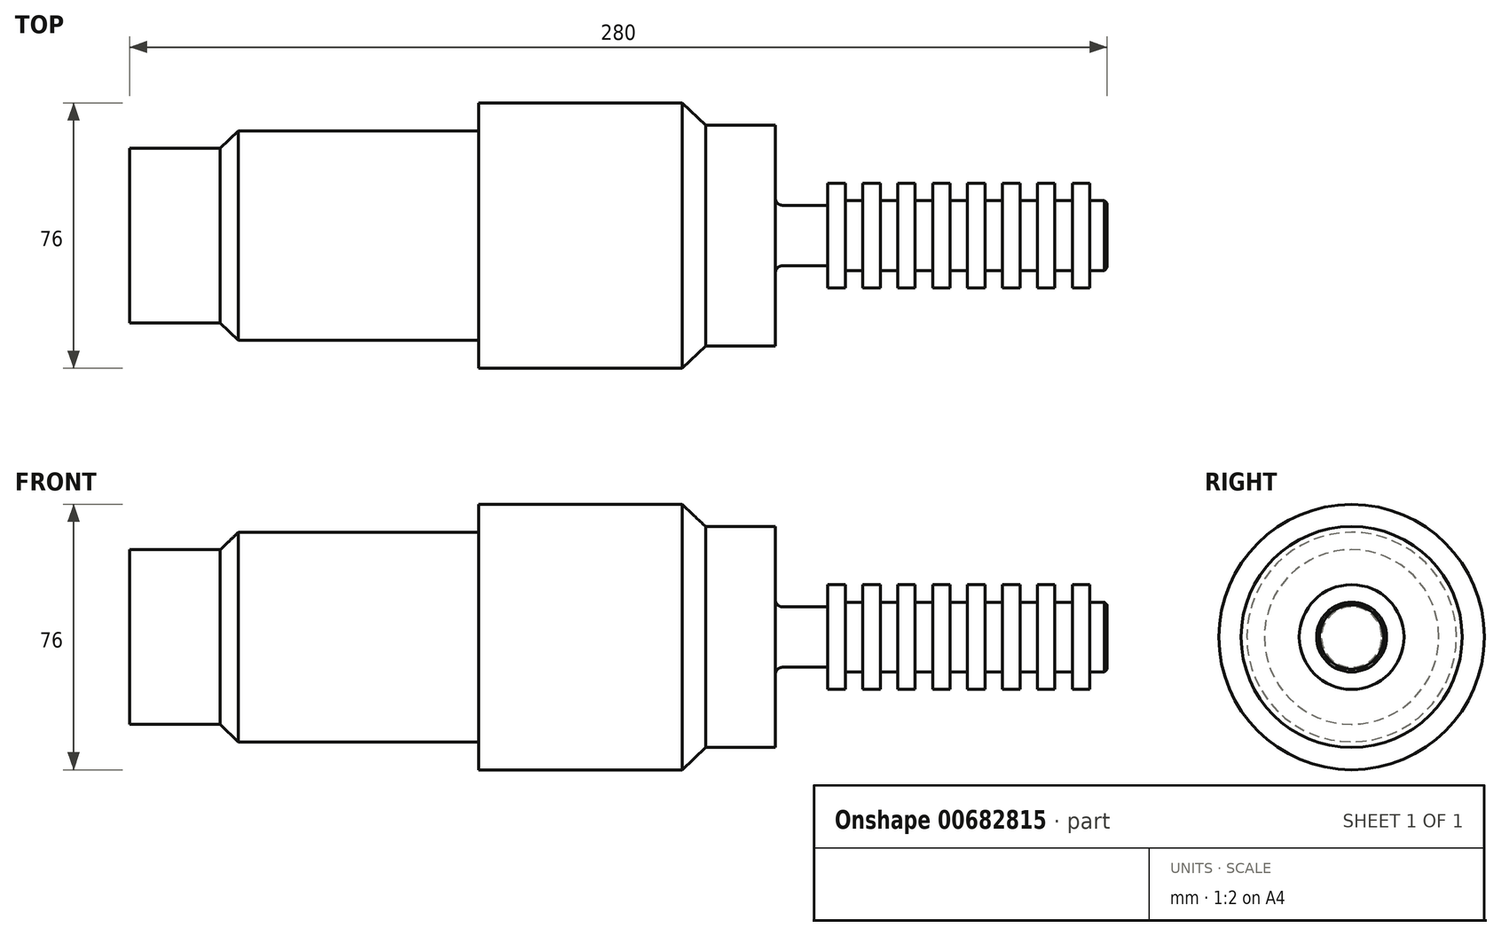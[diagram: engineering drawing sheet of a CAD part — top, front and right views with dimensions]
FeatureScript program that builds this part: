
annotation { "Feature Type Name" : "Feature", "Feature Type Description" : "" }
export const myFeature = defineFeature(function(context is Context, id is Id, definition is map)
    precondition{}
    {
        {
            var Q0;
            Q0=qCreatedBy(makeId("Front.planeOp"),FACE);
            var sketch = newSketch(context, id + "F0", { "sketchPlane" : qUnion([Q0])});
            skLineSegment(sketch, "E0", {"start": v(-57.6, 0) * mm, "end": v(222.4, 0) * mm});
            skLineSegment(sketch, "E1", {"start": v(-57.6, 0) * mm, "end": v(-57.6, 25) * mm});
            skLineSegment(sketch, "E2", {"start": v(-57.6, 25) * mm, "end": v(-31.6, 25) * mm});
            skLineSegment(sketch, "E3", {"start": v(-26.44, 30) * mm, "end": v(42.4, 30) * mm});
            skLineSegment(sketch, "E4", {"start": v(42.4, 30) * mm, "end": v(42.4, 38) * mm});
            skLineSegment(sketch, "E5", {"start": v(42.4, 38) * mm, "end": v(100.66, 38) * mm});
            skLineSegment(sketch, "E6", {"start": v(107.4, 31.64) * mm, "end": v(127.4, 31.64) * mm});
            skLineSegment(sketch, "E7", {"start": v(127.4, 31.64) * mm, "end": v(127.4, 15) * mm});
            skLineSegment(sketch, "E8", {"start": v(222.4, 9.2) * mm, "end": v(222.4, 0) * mm});
            skLineSegment(sketch, "E9", {"start": v(107.4, 31.64) * mm, "end": v(100.66, 38) * mm});
            skLineSegment(sketch, "E10", {"start": v(-31.6, 25) * mm, "end": v(-26.44, 30) * mm});
            skLineSegment(sketch, "E11", {"start": v(217.4, 15) * mm, "end": v(217.4, 10) * mm});
            skLineSegment(sketch, "E12", {"start": v(217.4, 10) * mm, "end": v(221.6, 10) * mm});
            skLineSegment(sketch, "E13", {"start": v(212.4, 15) * mm, "end": v(212.4, 10) * mm});
            skLineSegment(sketch, "E14", {"start": v(212.4, 10) * mm, "end": v(207.4, 10) * mm});
            skLineSegment(sketch, "E15", {"start": v(207.4, 10) * mm, "end": v(207.4, 15) * mm});
            skPoint(sketch, "E16.orphan", {"position": v(222.4, 15) * mm});
            skLineSegment(sketch, "E17.trimOffspring", {"start": v(212.4, 15) * mm, "end": v(217.4, 15) * mm});
            skLineSegment(sketch, "E18", {"start": v(202.4, 15) * mm, "end": v(202.4, 10) * mm});
            skLineSegment(sketch, "E19", {"start": v(202.4, 10) * mm, "end": v(197.4, 10) * mm});
            skLineSegment(sketch, "E20", {"start": v(197.4, 10) * mm, "end": v(197.4, 15) * mm});
            skLineSegment(sketch, "E21", {"start": v(192.4, 15) * mm, "end": v(192.4, 10) * mm});
            skLineSegment(sketch, "E22", {"start": v(192.4, 10) * mm, "end": v(187.4, 10) * mm});
            skLineSegment(sketch, "E23", {"start": v(187.4, 10) * mm, "end": v(187.4, 15) * mm});
            skLineSegment(sketch, "E24.top", {"start": v(182.4, 10) * mm, "end": v(177.4, 10) * mm});
            skLineSegment(sketch, "E24.left", {"start": v(182.4, 15) * mm, "end": v(182.4, 10) * mm});
            skLineSegment(sketch, "E24.right", {"start": v(177.4, 15) * mm, "end": v(177.4, 10) * mm});
            skLineSegment(sketch, "E25.top", {"start": v(172.4, 10) * mm, "end": v(167.4, 10) * mm});
            skLineSegment(sketch, "E25.left", {"start": v(172.4, 15) * mm, "end": v(172.4, 10) * mm});
            skLineSegment(sketch, "E25.right", {"start": v(167.4, 15) * mm, "end": v(167.4, 10) * mm});
            skLineSegment(sketch, "E26.top", {"start": v(162.4, 10) * mm, "end": v(157.4, 10) * mm});
            skLineSegment(sketch, "E26.left", {"start": v(162.4, 15) * mm, "end": v(162.4, 10) * mm});
            skLineSegment(sketch, "E26.right", {"start": v(157.4, 15) * mm, "end": v(157.4, 10) * mm});
            skLineSegment(sketch, "E27.top", {"start": v(152.4, 10) * mm, "end": v(147.4, 10) * mm});
            skLineSegment(sketch, "E27.left", {"start": v(152.4, 15) * mm, "end": v(152.4, 10) * mm});
            skLineSegment(sketch, "E27.right", {"start": v(147.4, 15) * mm, "end": v(147.4, 10) * mm});
            skLineSegment(sketch, "E28.trimOffspring", {"start": v(202.4, 15) * mm, "end": v(207.4, 15) * mm});
            skLineSegment(sketch, "E29.trimOffspring", {"start": v(192.4, 15) * mm, "end": v(197.4, 15) * mm});
            skLineSegment(sketch, "E30.trimOffspring", {"start": v(182.4, 15) * mm, "end": v(187.4, 15) * mm});
            skLineSegment(sketch, "E31.trimOffspring", {"start": v(172.4, 15) * mm, "end": v(177.4, 15) * mm});
            skLineSegment(sketch, "E32.trimOffspring", {"start": v(162.4, 15) * mm, "end": v(167.4, 15) * mm});
            skLineSegment(sketch, "E33.trimOffspring", {"start": v(152.4, 15) * mm, "end": v(157.4, 15) * mm});
            skLineSegment(sketch, "E34.top", {"start": v(142.4, 8.66) * mm, "end": v(138.75, 8.66) * mm});
            skLineSegment(sketch, "E34.left", {"start": v(142.4, 15) * mm, "end": v(142.4, 8.66) * mm});
            skLineSegment(sketch, "E35", {"start": v(127.4, 15) * mm, "end": v(127.4, 10.66) * mm});
            skLineSegment(sketch, "E36", {"start": v(129.4, 8.66) * mm, "end": v(138.75, 8.66) * mm});
            skLineSegment(sketch, "E37.trimOffspring", {"start": v(142.4, 15) * mm, "end": v(147.4, 15) * mm});
            skLineSegment(sketch, "E38", {"start": v(221.6, 10) * mm, "end": v(222.4, 9.2) * mm});
            skPoint(sketch, "E39.visualSharp", {"position": v(127.4, 8.66) * mm});
            skArc(sketch, "E39.filletArc", {"start": v(127.4, 10.66) * mm, "mid": v(128, 9.24) * mm, "end": v(129.4, 8.66) * mm});
            skLineSegment(sketch, "E40", {"start": v(202.4, 0) * mm, "end": v(202.6, 0.6) * mm});
            skLineSegment(sketch, "E41", {"start": v(197.4, 0) * mm, "end": v(197.57, 0.42) * mm});
            skSolve(sketch);
        }
        {
            var Q0;
            {var subQ0=sQuery(id+"F0.wireOp",EDGE,"E1");Q0=makeQuery(id+"F0.imprint","IMPRINT",FACE,{"disambiguationData":[TD([[makeQuery(id+"F0.imprint","IMPRINT",EDGE,{"derivedFrom":subQ0}),-1.0]])]});}
            var Q1;
            Q1=sQuery(id+"F0.wireOp",EDGE,"E0");
            revolve(context, id + "F1", {"surfaceOperationType" : NewSurfaceOperationType.NEW, "entities" : qUnion([Q0]), "axis" : qUnion([Q1]), "revolveType" : RevolveType.FULL});
        }
    });
